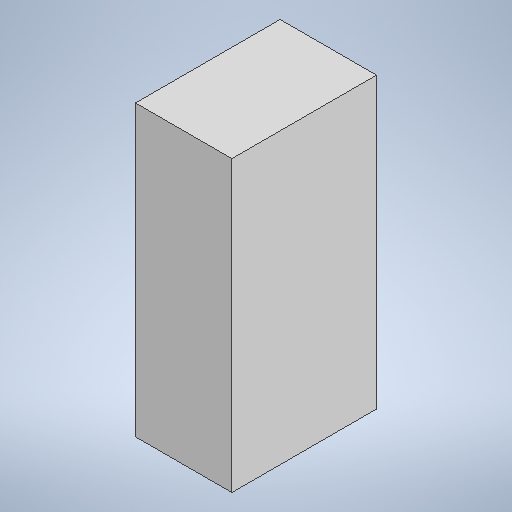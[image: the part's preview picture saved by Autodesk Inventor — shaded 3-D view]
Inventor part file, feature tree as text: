
AUTODESK INVENTOR PART (.ipt)
format: ipt  version: 2025 (Build 290162010, 162A)  size: 200,704 bytes
history: native  units: mm
features: extrude x1, sketch x1
ambient origin geometry x8: Origin, YZ Plane, XZ Plane, XY Plane, X Axis, Y Axis, Z Axis, Center Point
bodies: Solid1 (feature_tree)
feature tree (2):
  extrude  "Extrusion1"  Depth=600.0mm
  sketch  "Sketch1"  dims[d0=400.0mm d1=600.0mm d2=1200.0mm d3=0.0mm d4=0.5mm d5=0.872665mm]
